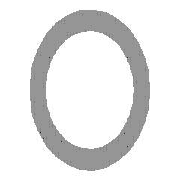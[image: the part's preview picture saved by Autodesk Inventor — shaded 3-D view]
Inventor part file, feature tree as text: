
AUTODESK INVENTOR PART (.ipt)
format: ipt  version: 2013 (Build 170138000, 138)  size: 108,544 bytes
history: native  units: mm (DEFAULTED — no unit token found)
features: other x4, sketch x3, plane x1
ambient origin geometry x8: Origin, YZ Plane, XZ Plane, XY Plane, X Axis, Y Axis, Z Axis, Center Point
bodies: Solid1 (feature_tree), Body (feature_tree)
feature tree (8):
  parser-record x1  (decoder bookkeeping rows leaked as tree rows — omitted from the tree; the rows remain in map.json)
  other  "Driven Length"
  other  "Start plane"
  other  "End plane"
  sketch  "Sketch"  dims[d2=762.0mm d3=0.0mm d4=-0.0mm d5=762.0mm d6=90.0deg d7=762.0mm]
  sketch  "Sketch3"  dims[d0=42.164mm]
  plane  "Work Plane3"
  sketch  "Sketch4"  dims[d1=3.556mm]
